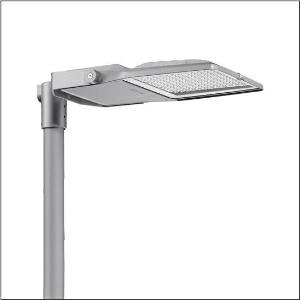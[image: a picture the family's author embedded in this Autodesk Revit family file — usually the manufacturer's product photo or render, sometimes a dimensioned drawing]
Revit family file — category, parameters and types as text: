
# Revit family: floodlight_fl_21_iq_midi___pl61_5xa7782e4c3a_83e0
name_source: partatom
category: Lighting Fixtures
units: mm (PartAtom-declared; Revit-internal decimal feet)

## family parameters
Cut with Voids When Loaded = No
Host = Face
Light Source = No
Part Type = Normal
Room Calculation Point = No
Round Connector Dimension = Use Diameter
Shared = No

## types (1)
- --- (1 x LED, 27490 lm, 208.1 W, 4000K)
    Apparent Load = 208 VA
    CIE Flux Codes = 33 65 98 100 100
    Color Rendering = 70
    Color Temperature = 4000K
    Default Elevation = 1800 mm
    Description = Floodlight FL 21 iQ midi, floodlight, primary light control with lens, of PMMA, primary optical cover: protective disc, of toughened safety glass, transparent, light distribution: PL61, light emission: direct distribution, installation type: surface-mounted, LED, High Power LED, rated luminous flux: 27.490lm, luminous efficacy: 132lm/W, light colour: 740, colour temperature: 4000K, control gear: ECG iQ, control: optimised constant luminous flux control (CLO 2.0), Desk-Remote (wireless, voltage-free reading and setting of iQ features in the workshop via application-optimized NFC function/RFID function), Smart-Wire, Night-Set, Temp-Guard, Auto-Match, Street-Remote, with terminal, 6-pole, mains connection: 220..240V, AC, 50/60Hz, start of lifetime: 208W, end of service life: 227W, reduction: 90W, luminaire housing, of diecast aluminium, powder-coated, Siteco® metallic grey (DB 702S), corrosivity category C5 mid according to DIN EN ISO 12944, sealing non-destructively replaceable, please order mast flange separately, mast bracket, of steel, galvanised, powder-coated, Siteco® metallic grey (DB 702S), protection rating (complete): IP66, insulation class (complete): insulation class II (safety insulation), certification: CE, protection symbol: D, impact resistance: IK08, permissible operating ambient temperature: -40..+40°C, permissible operating ambient temperature for outdoor applications: -40..+50°C, standard: DIN EN 12944, LABS conformity tested according to VDMA 24364:2018-05, packaging unit: 1 piece

Light Distribution: PL61
    Height = 76 mm
    Lamp = 1 x LED
    Lamp Light Flux = 27490 lm
    Lamp Power = 208.1 W
    Lamp count = 1
    Length = 657 mm
    Luminous efficacy = 132 lm/W
    Manufacturer = Siteco
    ModVariant = No
    Model = 5XA7782E4C3A
    Number of Poles = 1
    OnlyDefault = Yes
    Power Factor = 1
    Product Name = Floodlight FL 21 iQ midi | PL61
    Product group = floodlight | pylon annexe
    ProductGroupID = 6200
    Protection Class = Protection class II
    Protection Degree = IP 66
    RLX_Detail_Level = 1
    RLX_Emergency_Light_Flux = 0 lm
    RLX_Emergency_Type = 0
    RLX_Emergency_Type_DB = No
    RlxData = <blob elided: 153597 chars, md5=abd3204d>
    Socket = socket
    Standby Power = 0 W
    System Light Flux = 27490 lm
    System Power = 208 W
    Type Comments = factory setting: luminous flux: 100 % | dim-lin: 254 | 710 mA
    Type Image = l_1007123.jpg
    URL = http://relux.com
    VarID = @adj_056919
    Voltage = 0 V
    Weight = 0.00 kg
    Width = 442 mm

## geometry (parser evidence)
native form markers: Blend x4, Sweep x11
no freeform markers — native parametric forms only
